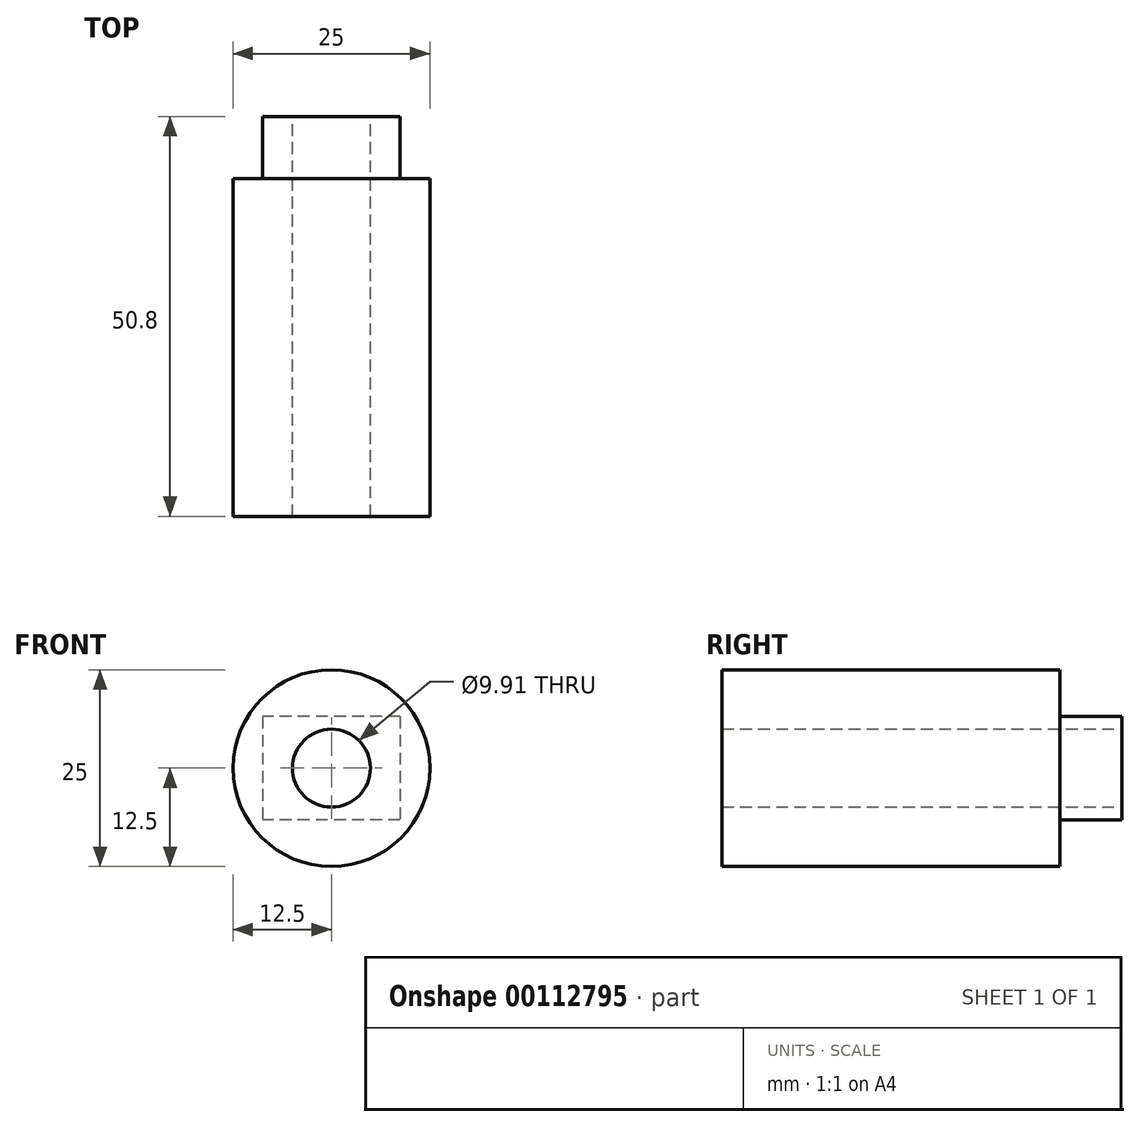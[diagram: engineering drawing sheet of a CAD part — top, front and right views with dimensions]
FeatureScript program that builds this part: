
annotation { "Feature Type Name" : "Feature", "Feature Type Description" : "" }
export const myFeature = defineFeature(function(context is Context, id is Id, definition is map)
    precondition{}
    {
        {
            var Q0;
            Q0=qCreatedBy(makeId("Front.planeOp"),FACE);
            cPlane(context, id + "F0", {"entities" : qUnion([Q0]), "cplaneType" : CPlaneType.OFFSET, "offset" : 7.9 * mm, "width" : 152.4 * mm, "height" : 152.4 * mm});
        }
        {
            var Q0;
            Q0=qCreatedBy(makeId("Front.planeOp"),FACE);
            var sketch = newSketch(context, id + "F1", { "sketchPlane" : qUnion([Q0])});
            skCircle(sketch, "E0", {"center": v(0, 0) * mm, "radius": 4.95 * mm});
            skSolve(sketch);
        }
        {
            var Q0;
            Q0=qCreatedBy(makeId("Front.planeOp"),FACE);
            var sketch = newSketch(context, id + "F2", { "sketchPlane" : qUnion([Q0])});
            skLineSegment(sketch, "E1.bottom", {"start": v(8.72, 6.54) * mm, "end": v(-8.72, 6.54) * mm});
            skLineSegment(sketch, "E1.top", {"start": v(8.72, -6.54) * mm, "end": v(-8.72, -6.54) * mm});
            skLineSegment(sketch, "E1.left", {"start": v(8.72, 6.54) * mm, "end": v(8.72, -6.54) * mm});
            skLineSegment(sketch, "E1.right", {"start": v(-8.72, 6.54) * mm, "end": v(-8.72, -6.54) * mm});
            skPoint(sketch, "E1.middle", {"position": v(0, 0) * mm});
            skSolve(sketch);
        }
        {
            var Q0;
            Q0=qCreatedBy(id+"F0.planeOp",FACE);
            var sketch = newSketch(context, id + "F3", { "sketchPlane" : qUnion([Q0])});
            skCircle(sketch, "E2", {"center": v(0, 0) * mm, "radius": 12.5 * mm});
            skSolve(sketch);
        }
        {
            var Q0;
            Q0=makeQuery(id+"F2.imprint","IMPRINT",FACE,{"disambiguationData":[TD([[makeQuery(id+"F2.imprint","IMPRINT",EDGE,{"derivedFrom":sQuery(id+"F2.wireOp",EDGE,"E1.bottom")}),1.0]])]});
            extrude(context, id + "F4", {"entities" : qUnion([Q0]), "depth" : 7.9 * mm});
        }
        {
            var Q0;
            Q0=makeQuery(id+"F3.imprint","IMPRINT",FACE,{"disambiguationData":[TD([[makeQuery(id+"F3.imprint","IMPRINT",EDGE,{"derivedFrom":sQuery(id+"F3.wireOp",EDGE,"E2")}),1.0]])]});
            extrude(context, id + "F5", {"entities" : qUnion([Q0]), "operationType" : NewBodyOperationType.ADD, "depth" : 42.9 * mm});
        }
        {
            var Q0;
            Q0=makeQuery(id+"F1.imprint","IMPRINT",FACE,{"disambiguationData":[TD([[makeQuery(id+"F1.imprint","IMPRINT",EDGE,{"derivedFrom":sQuery(id+"F1.wireOp",EDGE,"E0")}),1.0]])]});
            extrude(context, id + "F6", {"entities" : qUnion([Q0]), "operationType" : NewBodyOperationType.REMOVE, "depth" : 50.8 * mm});
        }
    });
